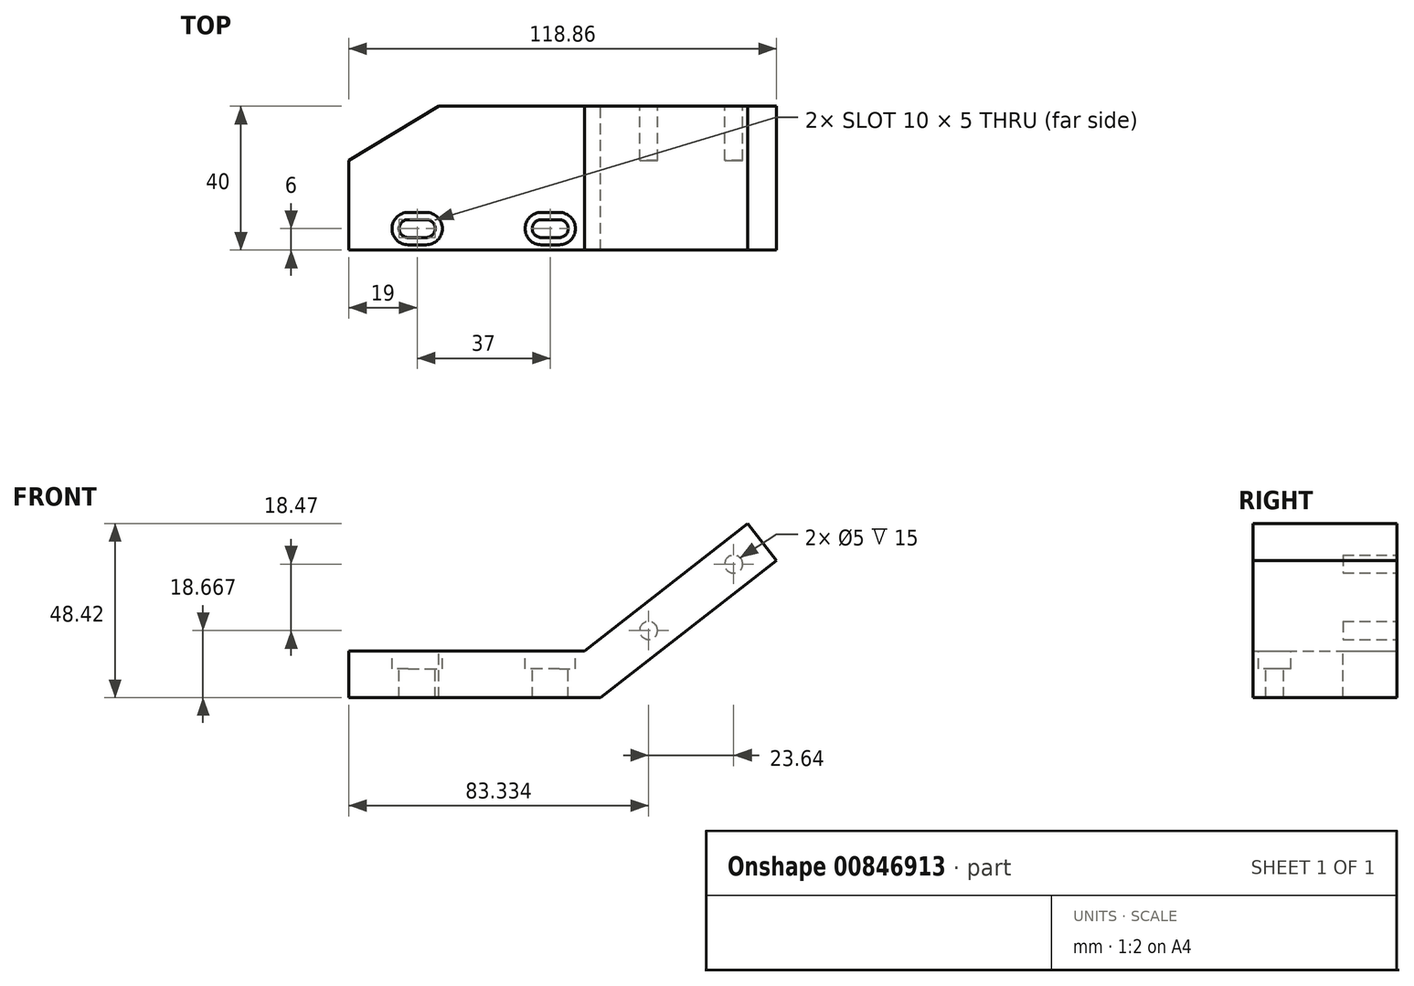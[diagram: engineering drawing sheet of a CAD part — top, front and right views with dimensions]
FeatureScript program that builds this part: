
annotation { "Feature Type Name" : "Feature", "Feature Type Description" : "" }
export const myFeature = defineFeature(function(context is Context, id is Id, definition is map)
    precondition{}
    {
        {
            var Q0;
            Q0=qCreatedBy(makeId("Front.planeOp"),FACE);
            var sketch = newSketch(context, id + "F0", { "sketchPlane" : qUnion([Q0])});
            skLineSegment(sketch, "E0", {"start": v(-70, 0) * mm, "end": v(0, 0) * mm});
            skLineSegment(sketch, "E1", {"start": v(0, 0) * mm, "end": v(48.86, 38.17) * mm});
            skPoint(sketch, "E2.start.orphan", {"position": v(44.27, 0) * mm});
            skLineSegment(sketch, "E3", {"start": v(-70, 0) * mm, "end": v(-70, 13) * mm});
            skLineSegment(sketch, "E4", {"start": v(-70, 13) * mm, "end": v(-4.48, 13) * mm});
            skLineSegment(sketch, "E5", {"start": v(48.86, 38.17) * mm, "end": v(40.85, 48.42) * mm});
            skLineSegment(sketch, "E6", {"start": v(40.85, 48.42) * mm, "end": v(-4.48, 13) * mm});
            skSolve(sketch);
        }
        {
            var Q0;
            Q0 = qSketchRegion(id + "F0", true);
            extrude(context, id + "F1", {"entities" : qUnion([Q0]), "depth" : 40 * mm, "offsetDistance" : 25 * mm});
        }
        {
            var Q0;
            Q0=makeQuery(id+"F1.opExtrude","SWEPT_FACE",FACE,{"disambiguationData":[OSD([sQuery(id+"F0.wireOp",EDGE,"E4")])]});
            var sketch = newSketch(context, id + "F2", { "sketchPlane" : qUnion([Q0])});
            skArc(sketch, "E7", {"start": v(-11.5, -38.5) * mm, "mid": v(-7, -34) * mm, "end": v(-11.5, -29.5) * mm});
            skArc(sketch, "E8", {"start": v(-53.5, -29.5) * mm, "mid": v(-58, -34) * mm, "end": v(-53.5, -38.5) * mm});
            skArc(sketch, "E9", {"start": v(-16.5, -29.5) * mm, "mid": v(-21, -34) * mm, "end": v(-16.5, -38.5) * mm});
            skArc(sketch, "E10", {"start": v(-48.5, -38.5) * mm, "mid": v(-44, -34) * mm, "end": v(-48.5, -29.5) * mm});
            skLineSegment(sketch, "E11", {"start": v(-11.5, -29.5) * mm, "end": v(-16.5, -29.5) * mm});
            skLineSegment(sketch, "E12", {"start": v(-16.5, -38.5) * mm, "end": v(-11.5, -38.5) * mm});
            skLineSegment(sketch, "E13", {"start": v(-53.5, -29.5) * mm, "end": v(-48.5, -29.5) * mm});
            skLineSegment(sketch, "E14", {"start": v(-48.5, -38.5) * mm, "end": v(-53.5, -38.5) * mm});
            skLineSegment(sketch, "E15", {"start": v(-53.5, -38.5) * mm, "end": v(-48.5, -38.5) * mm});
            skSolve(sketch);
        }
        {
            var Q0;
            Q0=makeQuery(id+"F2.imprint","IMPRINT",FACE,{"disambiguationData":[TD([[makeQuery(id+"F2.imprint","IMPRINT",EDGE,{"derivedFrom":sQuery(id+"F2.wireOp",EDGE,"E7")}),1.0]])]});
            var Q1;
            Q1=makeQuery(id+"F2.imprint","IMPRINT",FACE,{"disambiguationData":[TD([[makeQuery(id+"F2.imprint","IMPRINT",EDGE,{"derivedFrom":sQuery(id+"F2.wireOp",EDGE,"E8")}),1.0]])]});
            extrude(context, id + "F3", {"entities" : qUnion([Q0, Q1]), "operationType" : NewBodyOperationType.REMOVE, "oppositeDirection" : true, "depth" : 5 * mm, "offsetDistance" : 25 * mm});
        }
        {
            var Q0;
            Q0=makeQuery(id+"F1.opExtrude","SWEPT_FACE",FACE,{"disambiguationData":[OSD([sQuery(id+"F0.wireOp",EDGE,"E4")])]});
            var sketch = newSketch(context, id + "F4", { "sketchPlane" : qUnion([Q0])});
            skArc(sketch, "E16", {"start": v(-48.5, -36.5) * mm, "mid": v(-46, -34) * mm, "end": v(-48.5, -31.5) * mm});
            skArc(sketch, "E17", {"start": v(-53.5, -31.5) * mm, "mid": v(-56, -34) * mm, "end": v(-53.5, -36.5) * mm});
            skArc(sketch, "E18", {"start": v(-16.5, -31.5) * mm, "mid": v(-19, -34) * mm, "end": v(-16.5, -36.5) * mm});
            skArc(sketch, "E19", {"start": v(-11.5, -36.5) * mm, "mid": v(-9, -34) * mm, "end": v(-11.5, -31.5) * mm});
            skLineSegment(sketch, "E20", {"start": v(-53.5, -31.5) * mm, "end": v(-48.5, -31.5) * mm});
            skLineSegment(sketch, "E21", {"start": v(-48.5, -36.5) * mm, "end": v(-53.5, -36.5) * mm});
            skLineSegment(sketch, "E22", {"start": v(-16.5, -31.5) * mm, "end": v(-11.5, -31.5) * mm});
            skLineSegment(sketch, "E23", {"start": v(-11.5, -36.5) * mm, "end": v(-16.5, -36.5) * mm});
            skSolve(sketch);
        }
        {
            var Q0;
            Q0 = qSketchRegion(id + "F4", true);
            extrude(context, id + "F5", {"entities" : qUnion([Q0]), "operationType" : NewBodyOperationType.REMOVE, "oppositeDirection" : true, "depth" : 25 * mm, "offsetDistance" : 25 * mm});
        }
        {
            var Q0;
            Q0=makeQuery(id+"F1.opExtrude","SWEPT_FACE",FACE,{"disambiguationData":[OSD([sQuery(id+"F0.wireOp",EDGE,"E4")])]});
            var sketch = newSketch(context, id + "F6", { "sketchPlane" : qUnion([Q0])});
            skLineSegment(sketch, "E24", {"start": v(-70, -15) * mm, "end": v(-45, 0) * mm});
            skLineSegment(sketch, "E25", {"start": v(-45, 0) * mm, "end": v(-70, 0) * mm});
            skLineSegment(sketch, "E26", {"start": v(-70, 0) * mm, "end": v(-70, -15) * mm});
            skSolve(sketch);
        }
        {
            var Q0;
            Q0=makeQuery(id+"F6.imprint","IMPRINT",FACE,{"disambiguationData":[TD([[makeQuery(id+"F6.imprint","IMPRINT",EDGE,{"derivedFrom":sQuery(id+"F6.wireOp",EDGE,"E24")}),1.0]])]});
            extrude(context, id + "F7", {"entities" : qUnion([Q0]), "operationType" : NewBodyOperationType.REMOVE, "oppositeDirection" : true, "depth" : 25 * mm, "offsetDistance" : 25 * mm});
        }
        {
            var Q0;
            Q0=makeQuery(id+"F1.opExtrude","CAP_FACE",FACE,{"disambiguationData":[OSD([sQuery(id+"F0.wireOp",EDGE,"E0"),sQuery(id+"F0.wireOp",EDGE,"E1"),sQuery(id+"F0.wireOp",EDGE,"E3"),sQuery(id+"F0.wireOp",EDGE,"E4"),sQuery(id+"F0.wireOp",EDGE,"E5"),sQuery(id+"F0.wireOp",EDGE,"E6")])],"isStart":true});
            var sketch = newSketch(context, id + "F8", { "sketchPlane" : qUnion([Q0])});
            skCircle(sketch, "E27", {"center": v(-36.97, 37.14) * mm, "radius": 2.5 * mm});
            skCircle(sketch, "E28", {"center": v(-13.33, 18.67) * mm, "radius": 2.5 * mm});
            skSolve(sketch);
        }
        {
            var Q0;
            Q0=makeQuery(id+"F8.imprint","IMPRINT",FACE,{"disambiguationData":[TD([[makeQuery(id+"F8.imprint","IMPRINT",EDGE,{"derivedFrom":sQuery(id+"F8.wireOp",EDGE,"E27")}),1.0]])]});
            var Q1;
            Q1=makeQuery(id+"F8.imprint","IMPRINT",FACE,{"disambiguationData":[TD([[makeQuery(id+"F8.imprint","IMPRINT",EDGE,{"derivedFrom":sQuery(id+"F8.wireOp",EDGE,"E28")}),1.0]])]});
            extrude(context, id + "F9", {"entities" : qUnion([Q0, Q1]), "operationType" : NewBodyOperationType.REMOVE, "oppositeDirection" : true, "depth" : 15 * mm, "offsetDistance" : 25 * mm});
        }
    });
